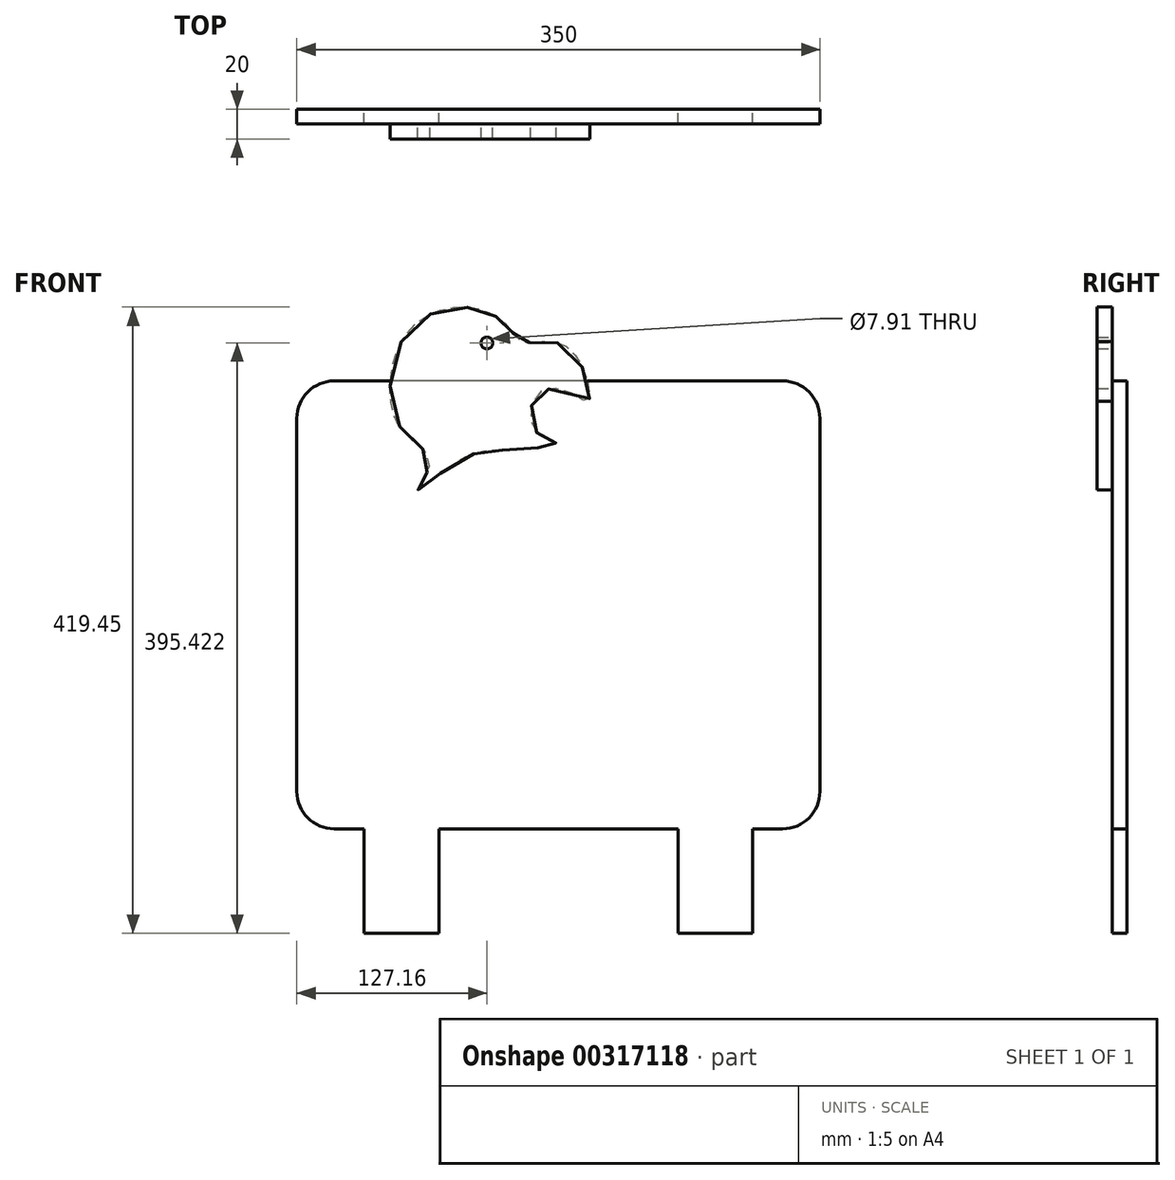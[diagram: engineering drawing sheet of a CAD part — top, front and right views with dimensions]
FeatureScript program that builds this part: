
annotation { "Feature Type Name" : "Feature", "Feature Type Description" : "" }
export const myFeature = defineFeature(function(context is Context, id is Id, definition is map)
    precondition{}
    {
        {
            var Q0;
            Q0=qCreatedBy(makeId("Front.planeOp"),FACE);
            cPlane(context, id + "F0", {"entities" : qUnion([Q0]), "cplaneType" : CPlaneType.OFFSET, "offset" : 240.87 * mm, "width" : 150 * mm, "height" : 150 * mm});
        }
        {
            var Q0;
            Q0=qCreatedBy(id+"F0.planeOp",FACE);
            var sketch = newSketch(context, id + "F1", { "sketchPlane" : qUnion([Q0])});
            skLineSegment(sketch, "E0.bottom", {"start": v(175, 100) * mm, "end": v(-175, 100) * mm});
            skLineSegment(sketch, "E0.top", {"start": v(175, 400) * mm, "end": v(-175, 400) * mm});
            skLineSegment(sketch, "E0.left", {"start": v(175, 100) * mm, "end": v(175, 400) * mm});
            skLineSegment(sketch, "E0.right", {"start": v(-175, 100) * mm, "end": v(-175, 400) * mm});
            skPoint(sketch, "E0.middle", {"position": v(0, 250) * mm});
            skLineSegment(sketch, "E1", {"start": v(0, 250) * mm, "end": v(0, 0) * mm, "construction": true});
            skLineSegment(sketch, "E2.bottom", {"start": v(-80, 30) * mm, "end": v(-130, 30) * mm});
            skLineSegment(sketch, "E2.top", {"start": v(-80, 100) * mm, "end": v(-130, 100) * mm, "construction": true});
            skLineSegment(sketch, "E2.left", {"start": v(-80, 30) * mm, "end": v(-80, 100) * mm});
            skLineSegment(sketch, "E2.right", {"start": v(-130, 30) * mm, "end": v(-130, 100) * mm});
            skLineSegment(sketch, "E3.MirrorCS", {"start": v(80, 30) * mm, "end": v(130, 30) * mm});
            skLineSegment(sketch, "E4.MirrorCS", {"start": v(80, 30) * mm, "end": v(80, 100) * mm});
            skLineSegment(sketch, "E5.MirrorCS", {"start": v(80, 100) * mm, "end": v(130, 100) * mm, "construction": true});
            skLineSegment(sketch, "E6.MirrorCS", {"start": v(130, 30) * mm, "end": v(130, 100) * mm});
            skSolve(sketch);
        }
        {
            var Q0;
            Q0 = qSketchRegion(id + "F1", true);
            extrude(context, id + "F2", {"entities" : qUnion([Q0]), "depth" : 10 * mm});
        }
        {
            var Q0;
            Q0=makeQuery(id+"F2.opExtrude","SWEPT_EDGE",EDGE,{"disambiguationData":[OSD([sQuery(id+"F1.wireOp",EDGE,"E0.top"),sQuery(id+"F1.wireOp",EDGE,"E0.right")])]});
            var Q1;
            Q1=makeQuery(id+"F2.opExtrude","SWEPT_EDGE",EDGE,{"disambiguationData":[OSD([sQuery(id+"F1.wireOp",EDGE,"E0.top"),sQuery(id+"F1.wireOp",EDGE,"E0.left")])]});
            var Q2;
            Q2=makeQuery(id+"F2.opExtrude","SWEPT_EDGE",EDGE,{"disambiguationData":[OSD([sQuery(id+"F1.wireOp",EDGE,"E0.bottom"),sQuery(id+"F1.wireOp",EDGE,"E0.left")])]});
            var Q3;
            Q3=makeQuery(id+"F2.opExtrude","SWEPT_EDGE",EDGE,{"disambiguationData":[OSD([sQuery(id+"F1.wireOp",EDGE,"E0.bottom"),sQuery(id+"F1.wireOp",EDGE,"E0.right")])]});
            fillet(context, id + "F3", {"entities" : qUnion([Q0, Q1, Q2, Q3]), "radius" : 25 * mm, "tangentPropagation" : true, "allowEdgeOverflow" : false});
        }
        {
            var Q0;
            Q0=makeQuery(id+"F2.opExtrude","CAP_FACE",FACE,{"disambiguationData":[OSD([sQuery(id+"F1.wireOp",EDGE,"E0.bottom"),sQuery(id+"F1.wireOp",EDGE,"E0.top"),sQuery(id+"F1.wireOp",EDGE,"E0.left"),sQuery(id+"F1.wireOp",EDGE,"E0.right"),sQuery(id+"F1.wireOp",EDGE,"E2.bottom"),sQuery(id+"F1.wireOp",EDGE,"E2.left"),sQuery(id+"F1.wireOp",EDGE,"E2.right"),sQuery(id+"F1.wireOp",EDGE,"E3.MirrorCS"),sQuery(id+"F1.wireOp",EDGE,"E4.MirrorCS"),sQuery(id+"F1.wireOp",EDGE,"E6.MirrorCS")])],"isStart":false});
            var sketch = newSketch(context, id + "F4", { "sketchPlane" : qUnion([Q0])});
            skFitSpline(sketch, "E7", {"points": [v(-106.4, 369.63) * mm, v(-100.4, 433.4) * mm, v(-54.12, 448.38) * mm, v(-32.3, 434.64) * mm, v(-22.44, 426.15) * mm, v(6.48, 422.26) * mm, v(20.37, 386.96) * mm, v(7.5, 392.42) * mm, v(-14.43, 390.6) * mm, v(-14.52, 365.23) * mm, v(-1.41, 358.2) * mm, v(-29.87, 353.94) * mm, v(-64.38, 347.8) * mm, v(-94.19, 327.17) * mm, v(-86, 345.53) * mm, v(-106.4, 369.63) * mm]});
            skCircle(sketch, "E8", {"center": v(-47.84, 425.42) * mm, "radius": 3.95 * mm});
            skSolve(sketch);
        }
        {
            var Q0;
            Q0 = qSketchRegion(id + "F4", true);
            extrude(context, id + "F5", {"entities" : qUnion([Q0]), "operationType" : NewBodyOperationType.ADD, "depth" : 10 * mm});
        }
    });
